# Revit family: Hager-Univers-IP43-D349-H598-Cl.II-Fire_res.encl_30min-NoHosted-DE-de
name_source: partatom
category: Equipement électrique
units: mm (PartAtom-declared; Revit-internal decimal feet)

## family parameters
Basée sur le plan de construction = Oui
Configuration du panneau = Deux colonnes, circuits au sein
Cote de connecteur circulaire = Utiliser le diamètre
Couper avec des vides une fois chargée = Non
Partagée = Non
Point de calcul de pièce = Non
Toujours verticalement = Oui
Type d'élément = Tableau de raccordement

## types (2) — shared parameters
Commentaires du type = Univers
EF000003 - Montageart = EV000384 - Aufputz
EF000007 - Farbe = EV000270 - grau
EF000040 - Höhe = 598 mm  [stored 1.96194 ft]
EF000049 - Tiefe = 349 mm  [stored 1.14501 ft]
EF000116 - RAL-Nummer = 7035
EF000118 - Mit Montageplatte = Non
EF000266 - Anzahl der Reihen = 3
EF000339 - Art der Abdeckung = EV004216 - Tür
EF001088 - Anbaumöglichkeit = Non
EF001131 - Innentiefe = 240 mm  [stored 0.787402 ft]
EF001596 - Werkstoff des Gehäuses = EV000139 - Kunststoff
EF001613 - Funktionserhalt = EV004178 - E30
EF003532 - Geeignet für Außengebrauch = Non
EF004293 - Schlagfestigkeit = EV008784 - IK10
EF004464 - Art der Tür = EV002646 - Einzel
EF006244 - Transparenter Deckel/Tür = Non
EF006306 - Mit Schloss = Oui
EF007800 - Geeignet für Blitzschutz = Non
EF008873 - Nennstrom (In) = 250 A
EF009170 - Materialstärke Gehäuse = 70 mm  [stored 0.229659 ft]
EF009171 - Materialstärke Tür/Deckel = 22 mm  [stored 0.0721785 ft]
EF009212 - Ausführung Deckel = EV000116 - geschlossen
EF015940 - Deckel mit Überdruckentlastung = Non
Elévation par défaut = 1219 mm
Fabricant = Hager
HG000002 - Mit tür = Oui
HG000003 - Bereich = Univers
HG000006 - Unterputz = Non
HG000009 - Doppelflügeligen Tür = Non
HG000010 - Asymmetrische Türen = Non
HG000023 - Gehäuse mit doppeltem Querschnitt = Non
HG000024 - Höhe des unteren Teils = 600 mm
HG000026 - Stehend auf dem Boden = Non
zero-valued in all types: EF000218 - Einbautiefe, HG000027 - Sockelhöhe

## per-type parameters (varying)
| type | EF000008 - Breite | EF000437 - Anzahl der Leitungseinführungen | EF002950 - Breite in Teilungseinheiten | EF004427 - Anzahl der Module | EF005474 - Schutzart (IP) | EF009554 - Anzahl der Öffnungen für Flanschplatten | HG000004 - Herstellerreferenz |
| Aufputz IP43 B398 H598 T349  - FB31LE | 398 mm  [stored 1.30577 ft] | 1 | 12 | 36 | EV006610 - IP43 | 2 | FB31LE |
| Aufputz IP44 B648 H598 T349  - FB32LE | 648 mm  [stored 2.12598 ft] | 2 | 24 | 72 | EV006418 - IP44 | 4 | FB32LE |

note: [stored X ft] marks values corroborated as IEEE doubles in the binary element streams (Revit-internal decimal feet)

## geometry (parser evidence)
native form markers: Blend x4, Sweep x5
no freeform markers — native parametric forms only
